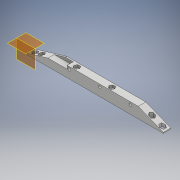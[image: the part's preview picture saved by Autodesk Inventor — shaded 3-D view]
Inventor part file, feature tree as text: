
AUTODESK INVENTOR PART (.ipt)
format: ipt  version: 2019 (Build 230136000, 136)  size: 267,776 bytes
history: native  units: mm
features: extrude x11, sketch x10, plane x7
ambient origin geometry x8: Origin, YZ Plane, XZ Plane, XY Plane, X Axis, Y Axis, Z Axis, Center Point
bodies: Solid1 (feature_tree)
feature tree (28):
  sketch  "Sketch1"  dims[d1=9.0mm d2=90.0deg]
  plane  "Work Plane2"
  sketch  "Sketch2"  dims[d4=3.2mm d6=3.2mm]
  plane  "Work Plane1"
  extrude  "klocek"  TaperAngle=90.0deg  [1 undecoded]
  plane  "Work Plane3"
  extrude  "prowadzenie osi"  Depth=3.2mm
  plane  "Work Plane4"
  sketch  "Sketch7"  dims[d9=60.5mm d13=3.2mm]
  sketch  "Sketch8"  dims[d15=3.2mm d17=3.2mm]
  extrude  "przedni skos"  Depth=42.0mm
  extrude  "tylni skos"  Depth=3.2mm
  plane  "Work Plane7"
  sketch  "Sketch5"  dims[d7=3.2mm d8=42.0mm]
  extrude  "hex insert middle"  Depth=3.2mm
  plane  "Work Plane6"
  sketch  "Sketch9"  dims[d18=36.5mm d26=3.2mm]
  extrude  "hex insert rear 1"  Depth=3.2mm
  plane  "Work Plane5"
  extrude  "hex insert rear 2"  Depth=3.2mm
  extrude  "hex insert front 1"  Depth=15.0mm
  extrude  "hex insert front 2"  Depth=11.0mm
  extrude  "ciecie przod"  Depth=5.9mm
  extrude  "sensor linii"  Depth=8.0mm
  sketch  "Sketch10"  dims[d27=48.0mm d28=3.2mm]
  sketch  "Sketch16"  dims[d29=42.0mm d32=15.0mm]
  sketch  "Sketch17"  dims[d33=5.0mm d38=11.0mm]
  sketch  "Sketch18"  dims[d39=0.0mm d61=3.2mm d62=8.0mm d63=12.5mm d64=52.0mm d65=36.5mm d67=13.0mm d68=0.0mm d70=7.5mm d71=0.0mm d77=5.0mm d78=0.0mm d80=12.0mm d81=30.0mm d82=3.0mm d83=0.0mm d84=8.5mm d85=0.0mm d86=12.0mm d87=40.0mm d88=7.0mm d89=0.0mm d91=9.0mm d92=0.0mm d93=5.9mm d94=9.0mm d95=0.0mm d96=10.0mm d97=0.0mm d98=5.9mm d99=5.9mm d100=5.9mm d102=4.0mm d103=25.0mm d104=2.5mm d105=7.3mm d106=0.0mm d108=4.0mm d109=4.0mm d110=4.0mm d111=4.0mm d112=4.0mm d113=4.0mm d114=10.0mm d115=73.0mm d118=5.9mm d122=2.0mm d123=5.9mm]
note: 1 required parameter value undecoded (feature->parameter linkage not recoverable at this tier; creation-order binding heuristic only, values carry confidence <= 0.55)
